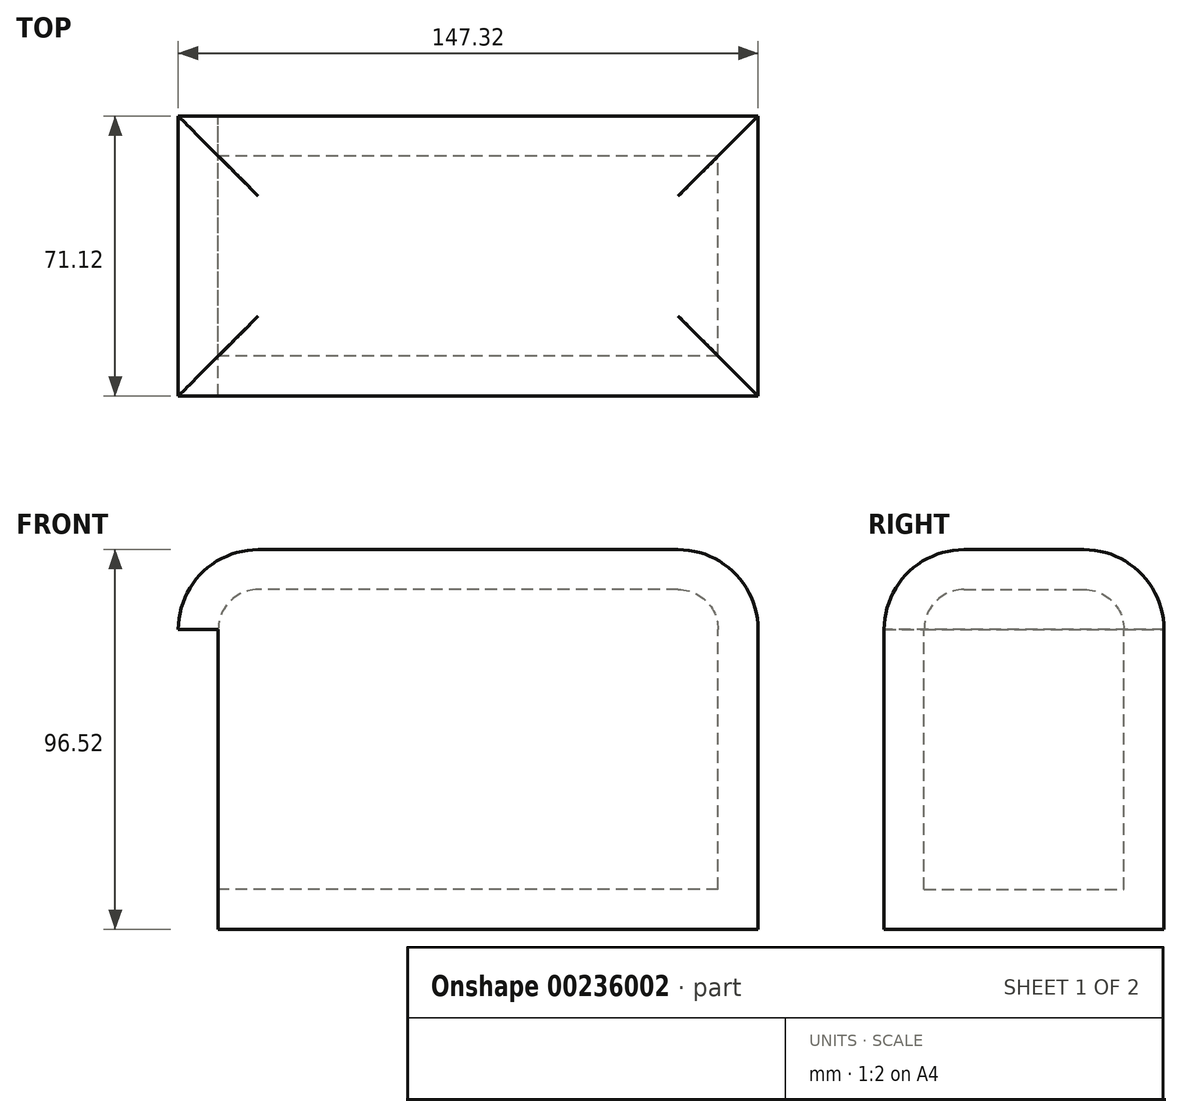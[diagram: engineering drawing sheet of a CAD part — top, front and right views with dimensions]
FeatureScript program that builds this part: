
annotation { "Feature Type Name" : "Feature", "Feature Type Description" : "" }
export const myFeature = defineFeature(function(context is Context, id is Id, definition is map)
    precondition{}
    {
        {
            var Q0;
            Q0=qCreatedBy(makeId("Front.planeOp"),FACE);
            var sketch = newSketch(context, id + "F0", { "sketchPlane" : qUnion([Q0])});
            skLineSegment(sketch, "E0.bottom", {"start": v(0, 0) * mm, "end": v(-127, 0) * mm});
            skLineSegment(sketch, "E0.top", {"start": v(0, 76.2) * mm, "end": v(-127, 76.2) * mm});
            skLineSegment(sketch, "E0.left", {"start": v(0, 0) * mm, "end": v(0, 76.2) * mm});
            skLineSegment(sketch, "E0.right", {"start": v(-127, 0) * mm, "end": v(-127, 76.2) * mm});
            skSolve(sketch);
        }
        {
            var Q0;
            Q0=makeQuery(id+"F0.imprint","IMPRINT",FACE,{"disambiguationData":[TD([[makeQuery(id+"F0.imprint","IMPRINT",EDGE,{"derivedFrom":sQuery(id+"F0.wireOp",EDGE,"E0.bottom")}),-1.0]])]});
            extrude(context, id + "F1", {"entities" : qUnion([Q0]), "endBound" : BoundingType.SYMMETRIC, "depth" : 50.8 * mm});
        }
        {
            var Q0;
            Q0=makeQuery(id+"F1.opExtrude","SWEPT_FACE",FACE,{"disambiguationData":[OSD([sQuery(id+"F0.wireOp",EDGE,"E0.top")])]});
            fillet(context, id + "F2", {"entities" : qUnion([Q0]), "radius" : 10.16 * mm, "tangentPropagation" : true, "allowEdgeOverflow" : false});
        }
        {
            var Q0;
            Q0=makeQuery(id+"F1.opExtrude","SWEPT_FACE",FACE,{"disambiguationData":[OSD([sQuery(id+"F0.wireOp",EDGE,"E0.right")])]});
            shell(context, id + "F3", {"entities" : qUnion([Q0]), "thickness" : 10.16 * mm, "oppositeDirection" : true});
        }
    });
